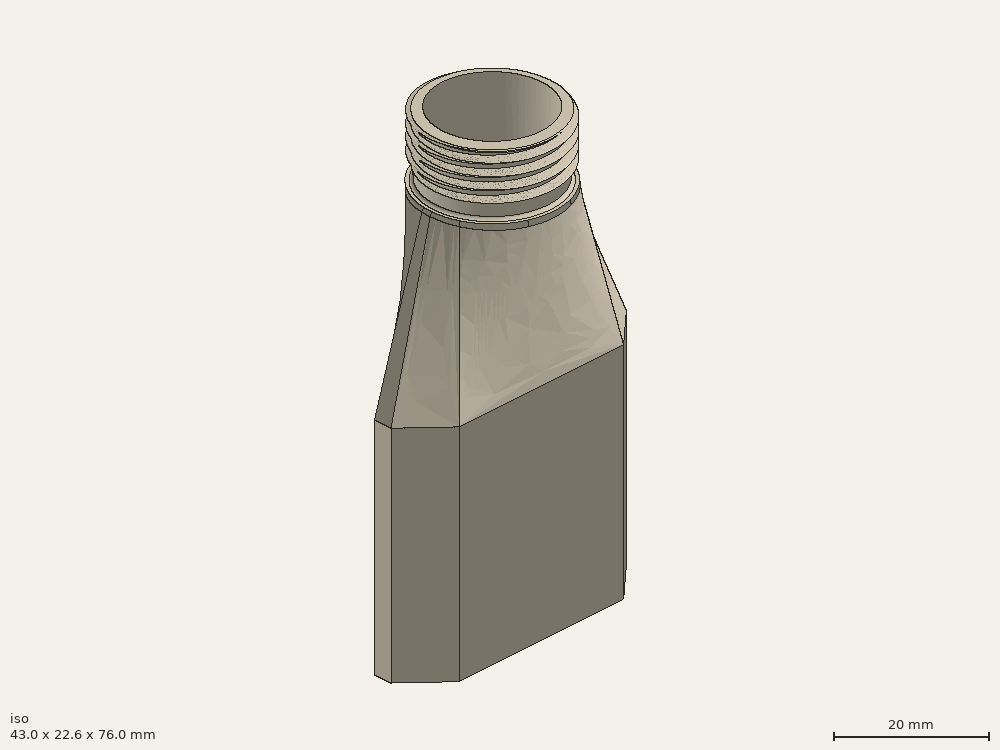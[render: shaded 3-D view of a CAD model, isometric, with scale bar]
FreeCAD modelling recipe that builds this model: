
FCSTD DOCUMENT  (FreeCAD 0.19R20514 (Git))
Label: tuboaspirador
License: All rights reserved
LicenseURL: http://en.wikipedia.org/wiki/All_rights_reserved
objects: Sketcher::SketchObject×4, PartDesign::Body×3, Part::MultiFuse×3, PartDesign::Pad×2, PartDesign::Thickness×1, Part::Part2DObjectPython×1, Part::Helix×1, PartDesign::ShapeBinder×1, Part::Sweep×1, Part::Cylinder×1, Part::Cut×1, PartDesign::AdditiveLoft×1, Part::Fillet×1
note: 25 computed .brp shape members not serialized (recipe doc carries the construction recipe); baked Part::Feature solids carry a one-line shape summary decoded from their .brp

FEATURE [Sketcher::SketchObject] Sketch
  MapMode = 5
  Support = -> [XY_Plane]
  sketch-geometry (7):
    g0: LineSegment StartX=-21.5 StartY=0 StartZ=0 EndX=-21.5 EndY=-3 EndZ=0
    g1: LineSegment StartX=-21.5 StartY=-3 StartZ=0 EndX=-15 EndY=-9 EndZ=0
    g2: LineSegment StartX=-15 StartY=-9 StartZ=0 EndX=15 EndY=-9 EndZ=0
    g3: LineSegment StartX=15 StartY=-9 StartZ=0 EndX=21.5 EndY=-3 EndZ=0
    g4: LineSegment StartX=21.5 StartY=-3 StartZ=0 EndX=21.5 EndY=-7.1e-15 EndZ=0
    g5: ArcOfCircle CenterX=3.6e-15 CenterY=-55.7812 CenterZ=0 NormalX=0 NormalY=0 NormalZ=1 AngleXU=0 Radius=59.7812 StartAngle=1.20291 EndAngle=1.93868
    g6: GeomPoint X=0 Y=4 Z=0
  constraints (18):
    c: Coincident(g0,g1)
    c: Coincident(g1,g2)
    c: Coincident(g2,g3)
    c: Coincident(g3,g4)
    c: PointOnObject(g4,g-1)
    c: Vertical(g4)
    c: Symmetric(g1,g2,g-2)
    c: Symmetric(g0,g4,g-2)
    c: Symmetric(g0,g3,g-2)
    c: DistanceX(g2,g2) = 30
    c: DistanceX(g0,g3) = 43
    c: DistanceY(g1,g0) = 9
    c: DistanceY(g1,g0) = 6
    c: Coincident(g5,g0)
    c: Coincident(g5,g4)
    c: PointOnObject(g6,g5)
    c: DistanceY(g2,g6) = 13
    c: PointOnObject(g6,g-2)
FEATURE [PartDesign::Pad] Pad
  Length = 38
  Length2 = 100
  Profile = -> Sketch
  Type = 0
FEATURE [PartDesign::Thickness] Thickness
  Base = -> Pad [Face8,Face7]
  BaseFeature = -> Pad
  Intersection = false
  Join = 0
  Mode = 0
  Reversed = true
  SupportTransform = true
  Value = 2
FEATURE [PartDesign::Body] Body  label="Aspirador"
  Group = -> [Sketch,Pad,Thickness]
  Origin = -> Origin
  Tip = -> Thickness
FEATURE [Sketcher::SketchObject] Sketch002
  MapMode = 5
  Support = -> [XY_Plane001]
  expr: Constraints[1] = (22 - 1.5) / 2
  sketch-geometry (1):
    g0: Circle CenterX=0 CenterY=0 CenterZ=0 NormalX=0 NormalY=0 NormalZ=1 AngleXU=0 Radius=10.25
  constraints (2):
    c: Coincident(g0,g-1)
    c: Radius(g0) = 10.25
FEATURE [PartDesign::Pad] Pad002
  Length = 10
  Length2 = 100
  Profile = -> Sketch002
  Type = 0
FEATURE [Part::Part2DObjectPython] VThreadProfile  # Draft 2D object (typed FeaturePython)
  Area = 350.15
  Closed = true
  Continuity = C2
  Instructions = Expand this with the ... button to view instructions | Sweep this object along a helix of the same pitch to produce your thread. | It is recommended to make the helix in the ThreadProfile workbench. | If there is an active Body the ThreadProfile object will be put into it.,If not it can be dragged and dropped into the body later. | If there is an active Body when the helix is made there will be made a ShapeBinder for it | For internal threads you will need to cut the Sweep object out of a cylinder, or if using Part Design sweep it as a Subtractive Pipe. | Always use Frenet mode | I have provided some presets, but it is possible there could be some errors.  Double check for mission critical applications. | Also, the tolerances might be different from what you wish to have.  I believe the internal minor diameters are all minimum and the external are all maximum.
  InternalOrExternal = 1
  MakeFace = true
  MinorDiameter = 20.2
  Parameterization = 1
  Pitch = 2
  Points = (719) [(10.0949,0.0882195,0),(10.0892,0.176353,0),(10.083,0.264399,0),(10.0761,0.352355,0),(10.0686,0.440218,0),(10.0605,0.527984,0),(10.0518,0.615651,0),+712 more]
  Presets = 89
  Quality = 1
  ThreadCount = 4
  Version = 1.51
  external_data = [-0.00235387,-0.00461052,-0.00677828,-0.00886428,-0.0108747,-0.0128149,-0.0146895,-0.0165028,-0.0182584,-0.0199597,-0.0216095,-0.0232106,-0.0247653,-0.0262759,-0.0277444,-0.0291725,-0.0305621,-0.0319145,-0.0332313,-0.0345138,-0.0357632,+698 more]
  internal_data = [0,0,0,0,0,0,0,0,0,0,0,0,0,0,0,0,0,0,0,0,0,0,0,0,0,0,0,0,0,0,0,0,0,0,0,0,0,0,0,0,0,0,0,0,0,0,0,0,0,0,0,0,0,0,0,0,0,0,0,0,0,0,0,0,0,0,0,0,0,0,0,0,0,0,0,0,0,0,0,0,0,0,0,0,0,0,0,0,0,0,0,0,0,0,0,0,0,0,0,0,0,0,0,0,0,0,0,0,0,0,0,0,0,0,0,0,0,0,0,0,+599 more]
  preset_names = <blob: 3959 chars omitted>
  presets_data = [0,0,0,2.20878,24.1173,24.6888,0.25,0.693,0.729,0.25,0.793,0.829,0.25,0.893,0.929,0.3,1.032,1.075,0.35,1.171,1.221,0.35,1.371,1.421,0.4,1.509,1.567,0.45,1.648,1.713,0.45,1.948,2.013,0.5,2.387,2.459,0.6,2.764,2.85,0.7,3.141,3.242,0.75,3.58,+712 more]
FEATURE [Part::Helix] Helix
  Angle = 0
  AttacherType = Attacher::AttachEngine3D
  Height = 8
  LocalCoord = 0
  Pitch = 2
  Radius = 10
  Style = 0
  expr: Pitch = VThreadProfile.Pitch
  expr: Height = VThreadProfile.ThreadCount * VThreadProfile.Pitch
  expr: .Placement.Base.x = VThreadProfile.Placement.Base.x
  expr: .Placement.Base.y = VThreadProfile.Placement.Base.y
  expr: .Placement.Base.z = VThreadProfile.Placement.Base.z
  expr: .Placement.Rotation.Angle = VThreadProfile.Placement.Rotation.Angle
  expr: .Placement.Rotation.Axis.x = VThreadProfile.Placement.Rotation.Axis.x
  expr: .Placement.Rotation.Axis.y = VThreadProfile.Placement.Rotation.Axis.y
  expr: .Placement.Rotation.Axis.z = VThreadProfile.Placement.Rotation.Axis.z
FEATURE [PartDesign::ShapeBinder] ShapeBinder
  Support = -> [Helix]
  TraceSupport = false
FEATURE [PartDesign::Body] Body001
  Group = -> [Sketch002,Pad002,VThreadProfile,ShapeBinder]
  Origin = -> Origin001
  Tip = -> Pad002
FEATURE [Part::Sweep] Sweep
  Frenet = true
  Placement = pos=(0,0,3) rot=(0,0,1;0rad)
  Sections = -> [VThreadProfile]
  Solid = true
  Spine = -> Helix [Edge1,Edge2,Edge3,Edge4]
  Transition = 1
FEATURE [Part::Cylinder] Cylinder  label="Cilindro"
  Angle = 360
  AttacherType = Attacher::AttachEngine3D
  Height = 15
  Placement = pos=(0,0,-3) rot=(0,0,1;0rad)
  Radius = 9
FEATURE [Part::MultiFuse] Fusion
  Shapes = -> [Body001,Sweep]
FEATURE [Part::Cut] Cut  label="rosca"
  Base = -> Fusion
  Placement = pos=(0,0,65) rot=(0,0,1;0rad)
  Tool = -> Cylinder
FEATURE [Sketcher::SketchObject] Sketch003
  AttachmentOffset = pos=(0,0,38) rot=(0,0,1;0rad)
  MapMode = 5
  Placement = pos=(0,0,38) rot=(0,0,1;0rad)
  Support = -> [XY_Plane002]
  sketch-geometry (14):
    g0: LineSegment StartX=-19.5 StartY=-1 StartZ=0 EndX=-19.5 EndY=-1.46154 EndZ=0
    g1: LineSegment StartX=-19.5 StartY=-1.46154 StartZ=0 EndX=-13.5 EndY=-7 EndZ=0
    g2: LineSegment StartX=-13.5 StartY=-7 StartZ=0 EndX=13.5 EndY=-7 EndZ=0
    g3: LineSegment StartX=13.5 StartY=-7 StartZ=0 EndX=19.5 EndY=-1.46154 EndZ=0
    g4: LineSegment StartX=19.5 StartY=-1.46154 StartZ=0 EndX=19.5 EndY=-1 EndZ=0
    g5: ArcOfCircle CenterX=0 CenterY=-62.875 CenterZ=0 NormalX=0 NormalY=0 NormalZ=1 AngleXU=0 Radius=64.875 StartAngle=1.2655 EndAngle=1.87609
    g6: GeomPoint X=0 Y=2 Z=0
    g7: LineSegment StartX=-21.5 StartY=-5.68e-14 StartZ=0 EndX=-21.5 EndY=-3 EndZ=0
    g8: LineSegment StartX=-21.5 StartY=-3 StartZ=0 EndX=-15 EndY=-9 EndZ=0
    g9: LineSegment StartX=-15 StartY=-9 StartZ=0 EndX=15 EndY=-9 EndZ=0
    g10: LineSegment StartX=15 StartY=-9 StartZ=0 EndX=21.5 EndY=-3 EndZ=0
    g11: LineSegment StartX=21.5 StartY=-3 StartZ=0 EndX=21.5 EndY=-6.39e-14 EndZ=0
    g12: ArcOfCircle CenterX=5.6e-15 CenterY=-55.7812 CenterZ=0 NormalX=0 NormalY=0 NormalZ=1 AngleXU=0 Radius=59.7812 StartAngle=1.20291 EndAngle=1.93868
    g13: GeomPoint X=0 Y=4 Z=0
  constraints (36):
    c: Coincident(g0,g1)
    c: Coincident(g1,g2)
    c: Coincident(g2,g3)
    c: Coincident(g3,g4)
    c: Vertical(g4)
    c: Symmetric(g1,g2,g-2)
    c: Symmetric(g0,g4,g-2)
    c: Symmetric(g0,g3,g-2)
    c: DistanceX(g2,g2) = 27
    c: DistanceX(g0,g3) = 39
    c: Coincident(g5,g0)
    c: Coincident(g5,g4)
    c: PointOnObject(g6,g5)
    c: PointOnObject(g6,g-2)
    c: Coincident(g7,g8)
    c: Coincident(g8,g9)
    c: Coincident(g9,g10)
    c: Coincident(g10,g11)
    c: Vertical(g11)
    c: DistanceX(g7,g10) = 43
    c: Coincident(g12,g7)
    c: Coincident(g12,g11)
    c: PointOnObject(g13,g12)
    c: DistanceY(g9,g13) = 13
    c: PointOnObject(g13,g-2)
    c: Symmetric(g8,g9,g-2)
    c: Symmetric(g7,g10,g-2)
    c: Symmetric(g7,g11,g-2)
    c: DistanceX(g9,g9) = 30
    c: DistanceY(g6,g13) = 2
    c: DistanceY(g9,g10) = 6
    c: DistanceY(g9,g11) = 9
    c: Parallel(g8,g1)
    c: DistanceY(g8,g1) = 2
    c: PointOnObject(g11,g-1)
    c: DistanceY(g1,g0) = 6
FEATURE [Sketcher::SketchObject] Sketch005
  AttachmentOffset = pos=(0,0,65) rot=(0,0,1;0rad)
  ExternalGeometry = -> [Sketch003]
  MapMode = 5
  Placement = pos=(0,0,65) rot=(0,0,1;0rad)
  Support = -> [XY_Plane002]
  sketch-geometry (2):
    g0: Circle CenterX=0 CenterY=0 CenterZ=0 NormalX=0 NormalY=0 NormalZ=1 AngleXU=0 Radius=9
    g1: Circle CenterX=0 CenterY=0 CenterZ=0 NormalX=0 NormalY=0 NormalZ=1 AngleXU=0 Radius=11.3
  constraints (4):
    c: Diameter(g0) = 18
    c: Coincident(g1,g0)
    c: Diameter(g1) = 22.6
    c: Coincident(g0,g-1)
FEATURE [PartDesign::AdditiveLoft] AdditiveLoft
  Closed = false
  Profile = -> Sketch003
  Ruled = false
  Sections = -> [Sketch005]
FEATURE [PartDesign::Body] Body002  label="tubo"
  Group = -> [Sketch003,Sketch005,AdditiveLoft]
  Origin = -> Origin002
  Tip = -> AdditiveLoft
FEATURE [Part::MultiFuse] Fusion001
  Shapes = -> [Cut,Body002]
FEATURE [Part::Fillet] Fillet001
  Base = -> Fusion001
  Edges = 7 edges: [Edge16 r=1,Edge19 r=1,Edge21 r=1,Edge23 r=1,Edge27 r=1,Edge28 r=1,Edge43 r=0.5]
FEATURE [Part::MultiFuse] Fusion002  label="Tubo Aspirador a bolsa"
  Shapes = -> [Fillet001,Body]
